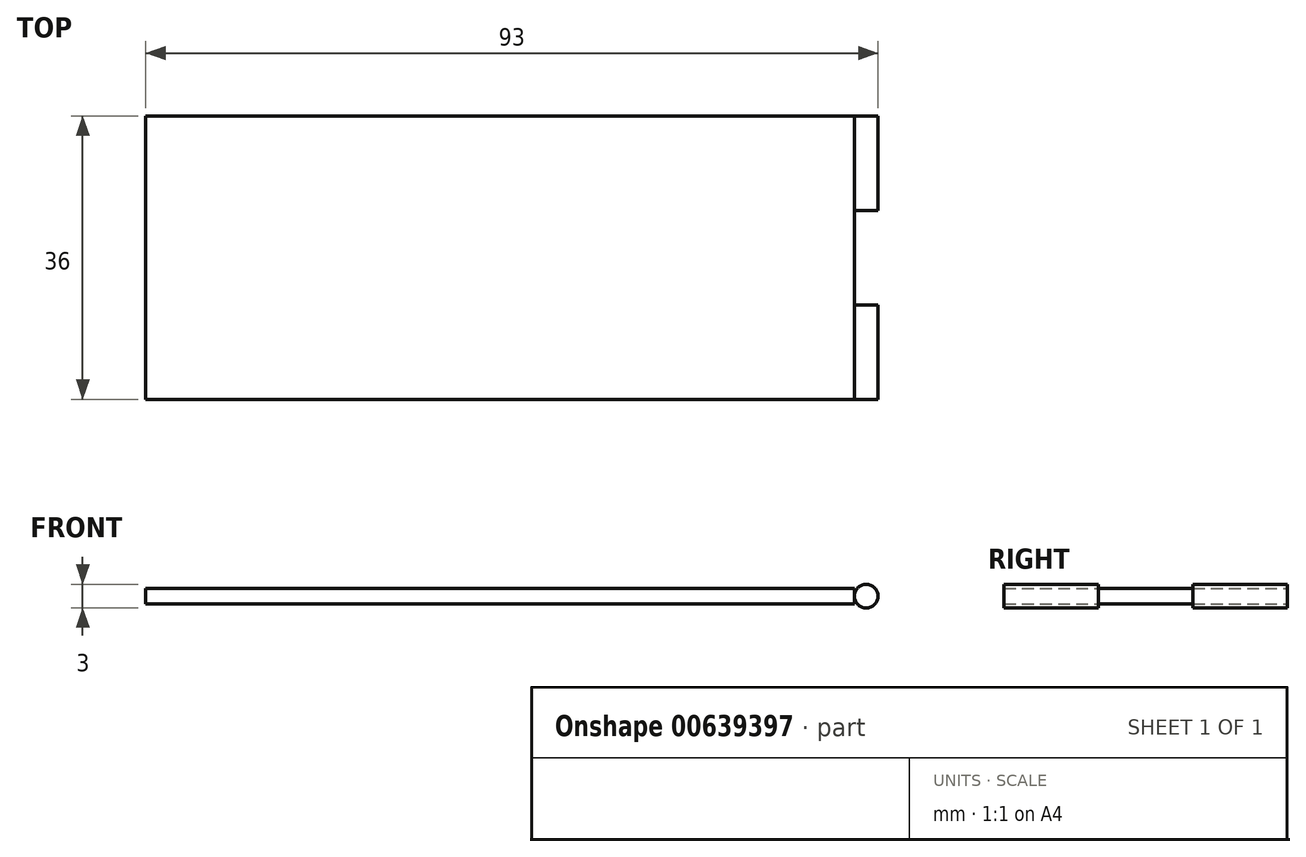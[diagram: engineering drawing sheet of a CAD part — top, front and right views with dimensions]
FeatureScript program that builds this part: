
annotation { "Feature Type Name" : "Feature", "Feature Type Description" : "" }
export const myFeature = defineFeature(function(context is Context, id is Id, definition is map)
    precondition{}
    {
        {
            var Q0;
            Q0=qCreatedBy(makeId("Top.planeOp"),FACE);
            var sketch = newSketch(context, id + "F0", { "sketchPlane" : qUnion([Q0])});
            skLineSegment(sketch, "E0.bottom", {"start": v(0, 0) * mm, "end": v(90, 0) * mm});
            skLineSegment(sketch, "E0.top", {"start": v(0, 36) * mm, "end": v(90, 36) * mm});
            skLineSegment(sketch, "E0.left", {"start": v(0, 0) * mm, "end": v(0, 36) * mm});
            skLineSegment(sketch, "E0.right", {"start": v(90, 0) * mm, "end": v(90, 36) * mm});
            skSolve(sketch);
        }
        {
            var Q0;
            Q0=makeQuery(id+"F0.imprint","IMPRINT",FACE,{"disambiguationData":[TD([[makeQuery(id+"F0.imprint","IMPRINT",EDGE,{"derivedFrom":sQuery(id+"F0.wireOp",EDGE,"E0.bottom")}),1.0]])]});
            extrude(context, id + "F1", {"entities" : qUnion([Q0]), "depth" : 2 * mm, "offsetDistance" : 25 * mm});
        }
        {
            var Q0;
            Q0=qCreatedBy(makeId("Front.planeOp"),FACE);
            var sketch = newSketch(context, id + "F2", { "sketchPlane" : qUnion([Q0])});
            skPoint(sketch, "E1.0", {"position": v(90, 1) * mm});
            skCircle(sketch, "E2", {"center": v(91.5, 1) * mm, "radius": 1.5 * mm});
            skSolve(sketch);
        }
        {
            var Q0;
            Q0=makeQuery(id+"F2.imprint","IMPRINT",FACE,{"disambiguationData":[TD([[makeQuery(id+"F2.imprint","IMPRINT",EDGE,{"derivedFrom":sQuery(id+"F2.wireOp",EDGE,"E2")}),1.0]])]});
            extrude(context, id + "F3", {"entities" : qUnion([Q0]), "oppositeDirection" : true, "depth" : 12 * mm, "offsetDistance" : 25 * mm});
        }
        {
            var Q0;
            Q0=makeQuery(id+"F1.opExtrude","SWEPT_FACE",FACE,{"disambiguationData":[OSD([sQuery(id+"F0.wireOp",EDGE,"E0.top")])]});
            var sketch = newSketch(context, id + "F4", { "sketchPlane" : qUnion([Q0])});
            skCircle(sketch, "E3.0", {"center": v(-91.5, 1) * mm, "radius": 1.5 * mm});
            skSolve(sketch);
        }
        {
            var Q0;
            Q0=makeQuery(id+"F4.imprint","IMPRINT",FACE,{"disambiguationData":[TD([[makeQuery(id+"F4.imprint","IMPRINT",EDGE,{"derivedFrom":sQuery(id+"F4.wireOp",EDGE,"E3.0")}),1.0]])]});
            extrude(context, id + "F5", {"entities" : qUnion([Q0]), "operationType" : NewBodyOperationType.ADD, "oppositeDirection" : true, "depth" : 12 * mm, "offsetDistance" : 25 * mm});
        }
    });
